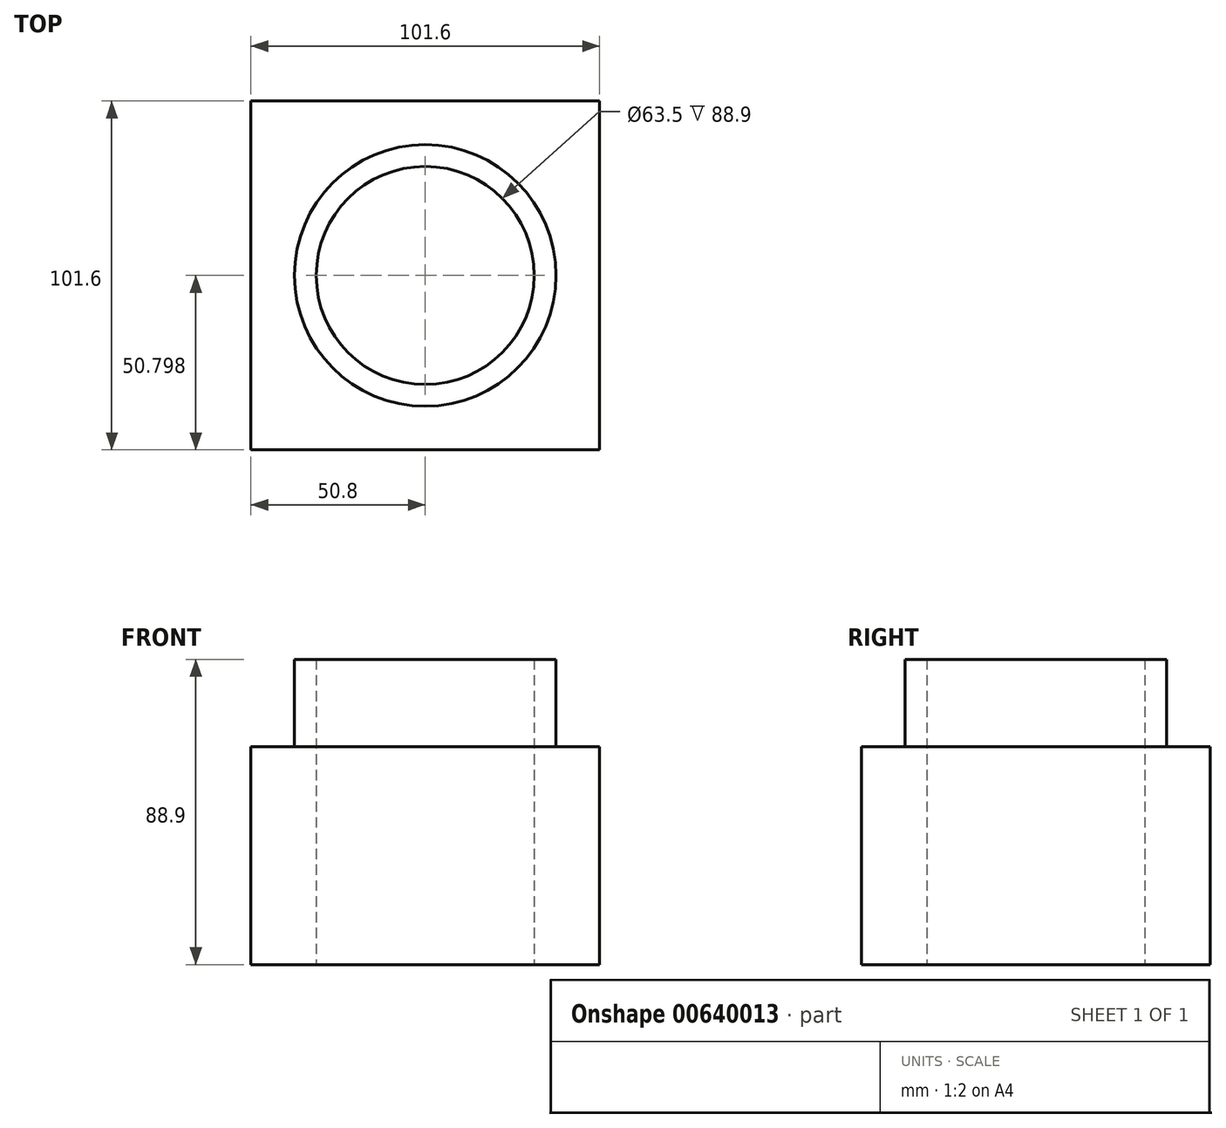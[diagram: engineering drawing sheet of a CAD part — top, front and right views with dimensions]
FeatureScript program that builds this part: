
annotation { "Feature Type Name" : "Feature", "Feature Type Description" : "" }
export const myFeature = defineFeature(function(context is Context, id is Id, definition is map)
    precondition{}
    {
        {
            var Q0;
            Q0=qCreatedBy(makeId("Top.planeOp"),FACE);
            var sketch = newSketch(context, id + "F0", { "sketchPlane" : qUnion([Q0])});
            skLineSegment(sketch, "E0.bottom", {"start": v(-62.32, 54.84) * mm, "end": v(39.28, 54.84) * mm});
            skLineSegment(sketch, "E0.top", {"start": v(-62.32, -46.76) * mm, "end": v(39.28, -46.76) * mm});
            skLineSegment(sketch, "E0.left", {"start": v(-62.32, 54.84) * mm, "end": v(-62.32, -46.76) * mm});
            skLineSegment(sketch, "E0.right", {"start": v(39.28, 54.84) * mm, "end": v(39.28, -46.76) * mm});
            skSolve(sketch);
        }
        {
            var Q0;
            Q0=makeQuery(id+"F0.imprint","IMPRINT",FACE,{"disambiguationData":[TD([[makeQuery(id+"F0.imprint","IMPRINT",EDGE,{"derivedFrom":sQuery(id+"F0.wireOp",EDGE,"E0.bottom")}),-1.0]])]});
            extrude(context, id + "F1", {"entities" : qUnion([Q0]), "depth" : 63.5 * mm, "offsetDistance" : 25.4 * mm});
        }
        {
            var Q0;
            Q0=makeQuery(id+"F1.opExtrude","CAP_FACE",FACE,{"disambiguationData":[OSD([sQuery(id+"F0.wireOp",EDGE,"E0.bottom"),sQuery(id+"F0.wireOp",EDGE,"E0.top"),sQuery(id+"F0.wireOp",EDGE,"E0.left"),sQuery(id+"F0.wireOp",EDGE,"E0.right")])],"isStart":false});
            var sketch = newSketch(context, id + "F2", { "sketchPlane" : qUnion([Q0])});
            skCircle(sketch, "E1", {"center": v(-11.52, 4.04) * mm, "radius": 31.75 * mm});
            skCircle(sketch, "E2", {"center": v(-11.52, 4.04) * mm, "radius": 38.1 * mm});
            skPoint(sketch, "E3.orphan", {"position": v(-11.52, 54.84) * mm});
            skPoint(sketch, "E4.orphan", {"position": v(-62.32, 4.04) * mm});
            skPoint(sketch, "E5.orphan", {"position": v(39.28, 4.04) * mm});
            skSolve(sketch);
        }
        {
            var Q0;
            Q0=makeQuery(id+"F2.imprint","IMPRINT",FACE,{"disambiguationData":[TD([[makeQuery(id+"F2.imprint","IMPRINT",EDGE,{"derivedFrom":sQuery(id+"F2.wireOp",EDGE,"E1")}),-1.0]])]});
            extrude(context, id + "F3", {"entities" : qUnion([Q0]), "operationType" : NewBodyOperationType.ADD, "depth" : 25.4 * mm, "offsetDistance" : 25.4 * mm});
        }
        {
            var Q0;
            Q0=makeQuery(id+"F3.boolean.opBoolean","SPLIT",FACE,{"disambiguationData":[TD([makeQuery(id+"F3.opExtrude","SWEPT_FACE",FACE,{"disambiguationData":[OSD([sQuery(id+"F2.wireOp",EDGE,"E1")])]})])],"derivedFrom":makeQuery(id+"F1.opExtrude","CAP_FACE",FACE,{"disambiguationData":[OSD([sQuery(id+"F0.wireOp",EDGE,"E0.bottom"),sQuery(id+"F0.wireOp",EDGE,"E0.top"),sQuery(id+"F0.wireOp",EDGE,"E0.left"),sQuery(id+"F0.wireOp",EDGE,"E0.right")])],"isStart":false})});
            extrude(context, id + "F4", {"entities" : qUnion([Q0]), "operationType" : NewBodyOperationType.REMOVE, "oppositeDirection" : true, "depth" : 63.5 * mm, "offsetDistance" : 25.4 * mm});
        }
    });
